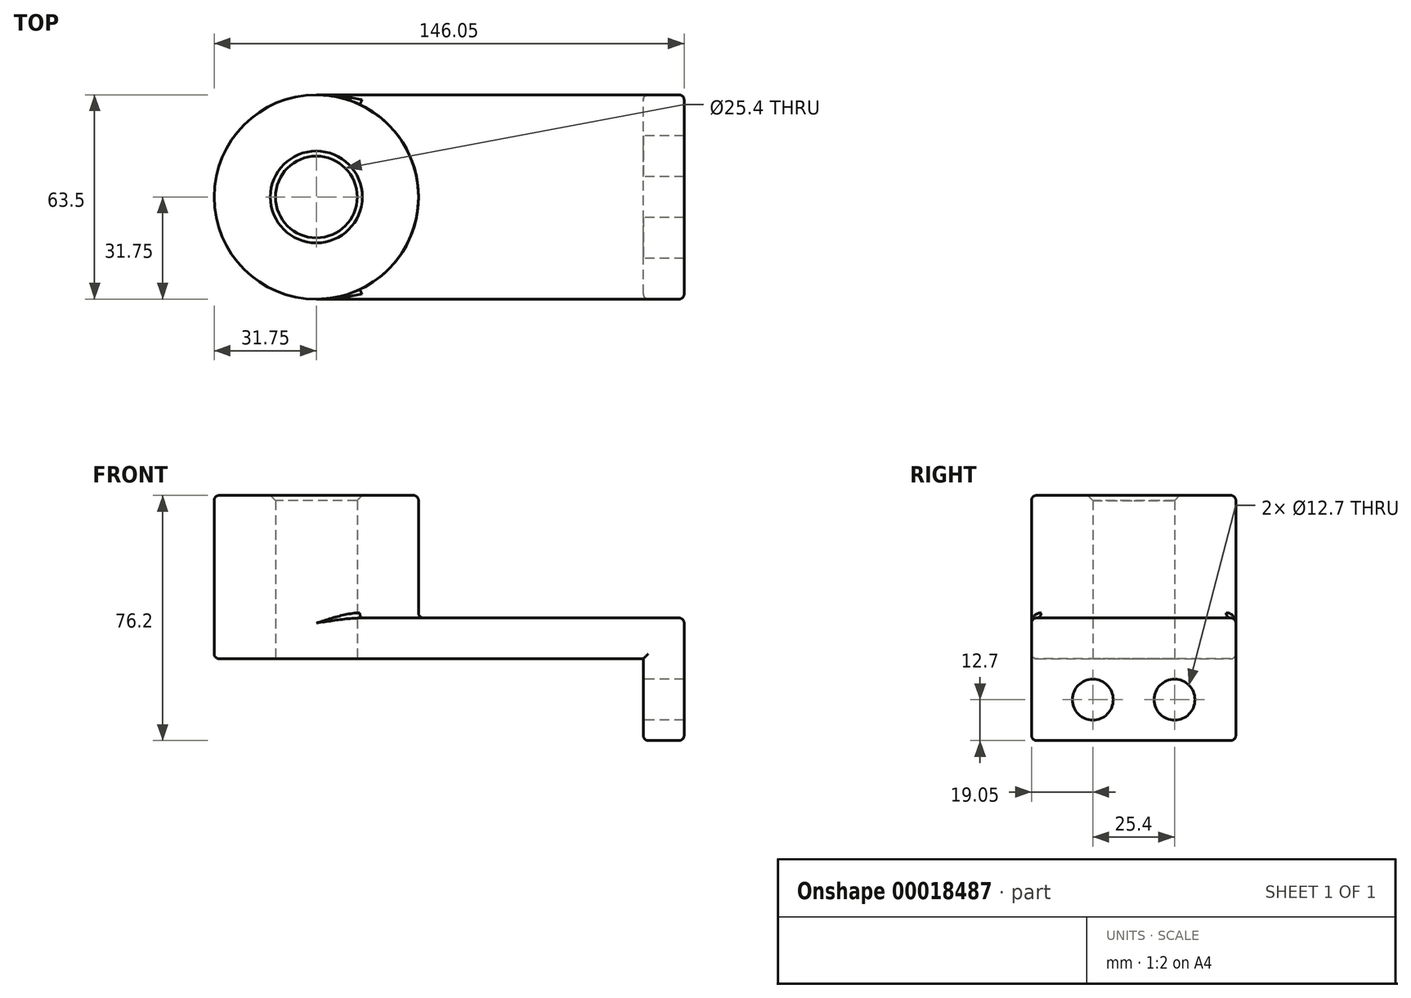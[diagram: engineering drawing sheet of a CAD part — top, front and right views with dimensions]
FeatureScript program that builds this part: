
annotation { "Feature Type Name" : "Feature", "Feature Type Description" : "" }
export const myFeature = defineFeature(function(context is Context, id is Id, definition is map)
    precondition{}
    {
        {
            var Q0;
            Q0=qCreatedBy(makeId("Top.planeOp"),FACE);
            var sketch = newSketch(context, id + "F0", { "sketchPlane" : qUnion([Q0])});
            skLineSegment(sketch, "E0.rect.bottom", {"start": v(38.1, -31.75) * mm, "end": v(-38.1, -31.75) * mm});
            skLineSegment(sketch, "E0.rect.top", {"start": v(38.1, 31.75) * mm, "end": v(-38.1, 31.75) * mm});
            skLineSegment(sketch, "E0.rect.left", {"start": v(38.1, -31.75) * mm, "end": v(38.1, 31.75) * mm});
            skLineSegment(sketch, "E0.rect.right", {"start": v(-38.1, -31.75) * mm, "end": v(-38.1, 31.75) * mm});
            skPoint(sketch, "E0.rect.middle", {"position": v(0, 0) * mm});
            skCircle(sketch, "E1", {"center": v(-38.1, 0) * mm, "radius": 31.75 * mm});
            skCircle(sketch, "E2", {"center": v(-38.1, 0) * mm, "radius": 12.7 * mm});
            skSolve(sketch);
        }
        {
            var Q0;
            {var subQ3=sQuery(id+"F0.wireOp",EDGE,"E0.rect.bottom");Q0=makeQuery(id+"F0.imprint","IMPRINT",FACE,{"disambiguationData":[TD([[makeQuery(id+"F0.imprint","IMPRINT",EDGE,{"derivedFrom":subQ3}),-1.0]])]});}
            var Q1;
            {var subQ0=sQuery(id+"F0.wireOp",EDGE,"E2");var subQ1=sQuery(id+"F0.wireOp",EDGE,"E0.rect.right");var subQ3=makeQuery(id+"F0.imprint","INTERSECT",VERTEX,{"disambiguationData":[OD(0.0)],"derivedFrom":[subQ1,subQ0]});Q1=makeQuery(id+"F0.imprint","IMPRINT",FACE,{"disambiguationData":[TD([[makeQuery(id+"F0.imprint","IMPRINT",EDGE,{"disambiguationData":[TD([[subQ3,1.0]])],"derivedFrom":subQ0}),-1.0]])]});}
            var Q2;
            {var subQ0=sQuery(id+"F0.wireOp",EDGE,"E2");var subQ1=sQuery(id+"F0.wireOp",EDGE,"E0.rect.right");var subQ3=makeQuery(id+"F0.imprint","INTERSECT",VERTEX,{"disambiguationData":[OD(0.0)],"derivedFrom":[subQ1,subQ0]});Q2=makeQuery(id+"F0.imprint","IMPRINT",FACE,{"disambiguationData":[TD([[makeQuery(id+"F0.imprint","IMPRINT",EDGE,{"disambiguationData":[TD([[subQ3,-1.0]])],"derivedFrom":subQ0}),-1.0]])]});}
            extrude(context, id + "F1", {"entities" : qUnion([Q0, Q1, Q2]), "depth" : 12.7 * mm});
        }
        {
            var Q0;
            {var subQ0=sQuery(id+"F0.wireOp",EDGE,"E2");var subQ1=sQuery(id+"F0.wireOp",EDGE,"E0.rect.right");var subQ3=makeQuery(id+"F0.imprint","INTERSECT",VERTEX,{"disambiguationData":[OD(0.0)],"derivedFrom":[subQ1,subQ0]});Q0=makeQuery(id+"F0.imprint","IMPRINT",FACE,{"disambiguationData":[TD([[makeQuery(id+"F0.imprint","IMPRINT",EDGE,{"disambiguationData":[TD([[subQ3,1.0]])],"derivedFrom":subQ0}),-1.0]])]});}
            var Q1;
            {var subQ0=sQuery(id+"F0.wireOp",EDGE,"E2");var subQ1=sQuery(id+"F0.wireOp",EDGE,"E0.rect.right");var subQ3=makeQuery(id+"F0.imprint","INTERSECT",VERTEX,{"disambiguationData":[OD(0.0)],"derivedFrom":[subQ1,subQ0]});Q1=makeQuery(id+"F0.imprint","IMPRINT",FACE,{"disambiguationData":[TD([[makeQuery(id+"F0.imprint","IMPRINT",EDGE,{"disambiguationData":[TD([[subQ3,-1.0]])],"derivedFrom":subQ0}),-1.0]])]});}
            extrude(context, id + "F2", {"entities" : qUnion([Q0, Q1]), "operationType" : NewBodyOperationType.ADD, "depth" : 50.8 * mm});
        }
        {
            var Q0;
            Q0=makeQuery(id+"F1.opExtrude","SWEPT_FACE",FACE,{"disambiguationData":[OSD([sQuery(id+"F0.wireOp",EDGE,"E0.rect.left")])]});
            extrude(context, id + "F3", {"entities" : qUnion([Q0]), "operationType" : NewBodyOperationType.ADD, "depth" : 25.4 * mm});
        }
        {
            var Q0;
            Q0=makeQuery(id+"F3.opExtrude","CAP_FACE",FACE,{"disambiguationData":[OSD([sQuery(id+"F0.wireOp",EDGE,"E0.rect.left")])],"isStart":false});
            var sketch = newSketch(context, id + "F4", { "sketchPlane" : qUnion([Q0])});
            skLineSegment(sketch, "E3.bottom", {"start": v(-31.75, 12.7) * mm, "end": v(31.75, 12.7) * mm});
            skLineSegment(sketch, "E3.top", {"start": v(-31.75, -25.4) * mm, "end": v(31.75, -25.4) * mm});
            skLineSegment(sketch, "E3.left", {"start": v(-31.75, 12.7) * mm, "end": v(-31.75, -25.4) * mm});
            skLineSegment(sketch, "E3.right", {"start": v(31.75, 12.7) * mm, "end": v(31.75, -25.4) * mm});
            skLineSegment(sketch, "E4", {"start": v(0, 0) * mm, "end": v(0, -25.4) * mm});
            skCircle(sketch, "E5", {"center": v(-12.7, -12.7) * mm, "radius": 6.35 * mm});
            skCircle(sketch, "E6.MirrorC", {"center": v(12.7, -12.7) * mm, "radius": 6.35 * mm});
            skSolve(sketch);
        }
        {
            var Q0;
            Q0 = qSketchRegion(id + "F4", true);
            extrude(context, id + "F5", {"entities" : qUnion([Q0]), "operationType" : NewBodyOperationType.ADD, "depth" : 12.7 * mm});
        }
        {
            var Q0;
            {var subQ0=sQuery(id+"F0.wireOp",EDGE,"E1");Q0=makeQuery(id+"F2.boolean.opBoolean","INTERSECT",EDGE,{"derivedFrom":[makeQuery(id+"F1.opExtrude","CAP_FACE",FACE,{"disambiguationData":[OSD([sQuery(id+"F0.wireOp",EDGE,"E0.rect.bottom"),sQuery(id+"F0.wireOp",EDGE,"E0.rect.top"),sQuery(id+"F0.wireOp",EDGE,"E0.rect.left"),subQ0,sQuery(id+"F0.wireOp",EDGE,"E2")])],"isStart":false}),makeQuery(id+"F2.opExtrude","SWEPT_FACE",FACE,{"disambiguationData":[OSD([subQ0])]})]});}
            var Q1;
            Q1=makeQuery(id+"F5.opExtrude","CAP_EDGE",EDGE,{"disambiguationData":[OSD([sQuery(id+"F4.wireOp",EDGE,"E3.bottom")])],"isStart":false});
            var Q2;
            Q2=makeQuery(id+"F5.opExtrude","SWEPT_EDGE",EDGE,{"disambiguationData":[OSD([sQuery(id+"F4.wireOp",EDGE,"E3.top"),sQuery(id+"F4.wireOp",EDGE,"E3.left")])]});
            var Q3;
            Q3=makeQuery(id+"F5.opExtrude","SWEPT_EDGE",EDGE,{"disambiguationData":[OSD([sQuery(id+"F4.wireOp",EDGE,"E3.top"),sQuery(id+"F4.wireOp",EDGE,"E3.right")])]});
            var Q4;
            {var subQ0=sQuery(id+"F0.wireOp",EDGE,"E0.rect.bottom");var subQ1=sQuery(id+"F0.wireOp",EDGE,"E0.rect.left");Q4=makeQuery(id+"F5.boolean.opBoolean","MERGE",EDGE,{"derivedFrom":[makeQuery(id+"F3.boolean.opBoolean","MERGE",EDGE,{"derivedFrom":[makeQuery(id+"F1.opExtrude","CAP_EDGE",EDGE,{"disambiguationData":[OSD([subQ0])],"isStart":false}),makeQuery(id+"F3.opExtrude","SWEPT_EDGE",EDGE,{"disambiguationData":[OSD([subQ0,subQ1]),TDD([makeQuery(id+"F1.opExtrude","CAP_VERTEX",VERTEX,{"disambiguationData":[OSD([subQ0,subQ1])],"isStart":false})])]})]}),makeQuery(id+"F5.opExtrude","SWEPT_EDGE",EDGE,{"disambiguationData":[OSD([sQuery(id+"F4.wireOp",EDGE,"E3.bottom"),sQuery(id+"F4.wireOp",EDGE,"E3.left")])]})]});}
            var Q5;
            {var subQ0=sQuery(id+"F0.wireOp",EDGE,"E0.rect.bottom");var subQ1=sQuery(id+"F0.wireOp",EDGE,"E0.rect.left");Q5=makeQuery(id+"F3.boolean.opBoolean","MERGE",EDGE,{"derivedFrom":[makeQuery(id+"F1.opExtrude","CAP_EDGE",EDGE,{"disambiguationData":[OSD([subQ0])],"isStart":true}),makeQuery(id+"F3.opExtrude","SWEPT_EDGE",EDGE,{"disambiguationData":[OSD([subQ0,subQ1]),TDD([makeQuery(id+"F1.opExtrude","CAP_VERTEX",VERTEX,{"disambiguationData":[OSD([subQ0,subQ1])],"isStart":true})])]})]});}
            var Q6;
            {var subQ0=sQuery(id+"F0.wireOp",EDGE,"E0.rect.top");var subQ1=sQuery(id+"F0.wireOp",EDGE,"E0.rect.left");Q6=makeQuery(id+"F5.boolean.opBoolean","MERGE",EDGE,{"derivedFrom":[makeQuery(id+"F3.boolean.opBoolean","MERGE",EDGE,{"derivedFrom":[makeQuery(id+"F1.opExtrude","CAP_EDGE",EDGE,{"disambiguationData":[OSD([subQ0])],"isStart":false}),makeQuery(id+"F3.opExtrude","SWEPT_EDGE",EDGE,{"disambiguationData":[OSD([subQ0,subQ1]),TDD([makeQuery(id+"F1.opExtrude","CAP_VERTEX",VERTEX,{"disambiguationData":[OSD([subQ0,subQ1])],"isStart":false})])]})]}),makeQuery(id+"F5.opExtrude","SWEPT_EDGE",EDGE,{"disambiguationData":[OSD([sQuery(id+"F4.wireOp",EDGE,"E3.bottom"),sQuery(id+"F4.wireOp",EDGE,"E3.right")])]})]});}
            fillet(context, id + "F6", {"entities" : qUnion([Q0, Q1, Q2, Q3, Q4, Q5, Q6]), "radius" : 1.59 * mm, "tangentPropagation" : true, "allowEdgeOverflow" : false});
        }
        {
            var Q0;
            Q0=makeQuery(id+"F5.opExtrude","CAP_EDGE",EDGE,{"disambiguationData":[OSD([sQuery(id+"F4.wireOp",EDGE,"E3.left")])],"isStart":false});
            var Q1;
            Q1=makeQuery(id+"F5.opExtrude","CAP_EDGE",EDGE,{"disambiguationData":[OSD([sQuery(id+"F4.wireOp",EDGE,"E3.left")])],"isStart":true});
            var Q2;
            Q2=makeQuery(id+"F2.opExtrude","CAP_EDGE",EDGE,{"disambiguationData":[OSD([sQuery(id+"F0.wireOp",EDGE,"E1")])],"isStart":false});
            fillet(context, id + "F7", {"entities" : qUnion([Q0, Q1, Q2]), "radius" : 1.59 * mm, "tangentPropagation" : true, "allowEdgeOverflow" : false});
        }
        {
            var Q0;
            Q0=makeQuery(id+"F2.opExtrude","CAP_EDGE",EDGE,{"disambiguationData":[OSD([sQuery(id+"F0.wireOp",EDGE,"E2")])],"isStart":false});
            chamfer(context, id + "F8", {"entities" : qUnion([Q0]), "width" : 1.59 * mm, "tangentPropagation" : true});
        }
    });
